# Revit family: Shower-Valve_Trim-KOHLER-Coralais-K-TS15621
name_source: partatom
category: Specialty Equipment
revit_build: Autodesk Revit 2015 (Build: 20140606_1530(x64)
units: mm (PartAtom-declared; Revit-internal decimal feet)

## types (2) — shared parameters
ADA Compliant = Yes
Assembly Code = C1030200
Date Modified = 03/19/2018
Default Elevation = 42"
Description = Rite-Temp valve trim with lever handle
Height = 6 1/2"
Length = 2 7/8"
Manufacturer = KOHLER Co.
MasterFormat 1995 = 10820
MasterFormat 2004 = 10.28.13
Material = Premium Metal Construction
Product Documentation Link = http://www.us.kohler.com
Product Name = Coralais
Product Page URL = http://www.us.kohler.com
URL = https://www.us.kohler.com
Width = 6 1/2"

## per-type parameters (varying)
| type | Finish | Model | Type |
| CP- Polished Chrome | Kohler-Metal-CP-Polished_Chrome | K-TS15621-4-CP | 1 |
| G- Brushed Chrome | Kohler-Metal-G-Brushed_Chrome | K-TS15621-4-G | 2 |

## geometry (parser evidence)
native form markers: Blend x2, Sweep x5
no freeform markers — native parametric forms only
